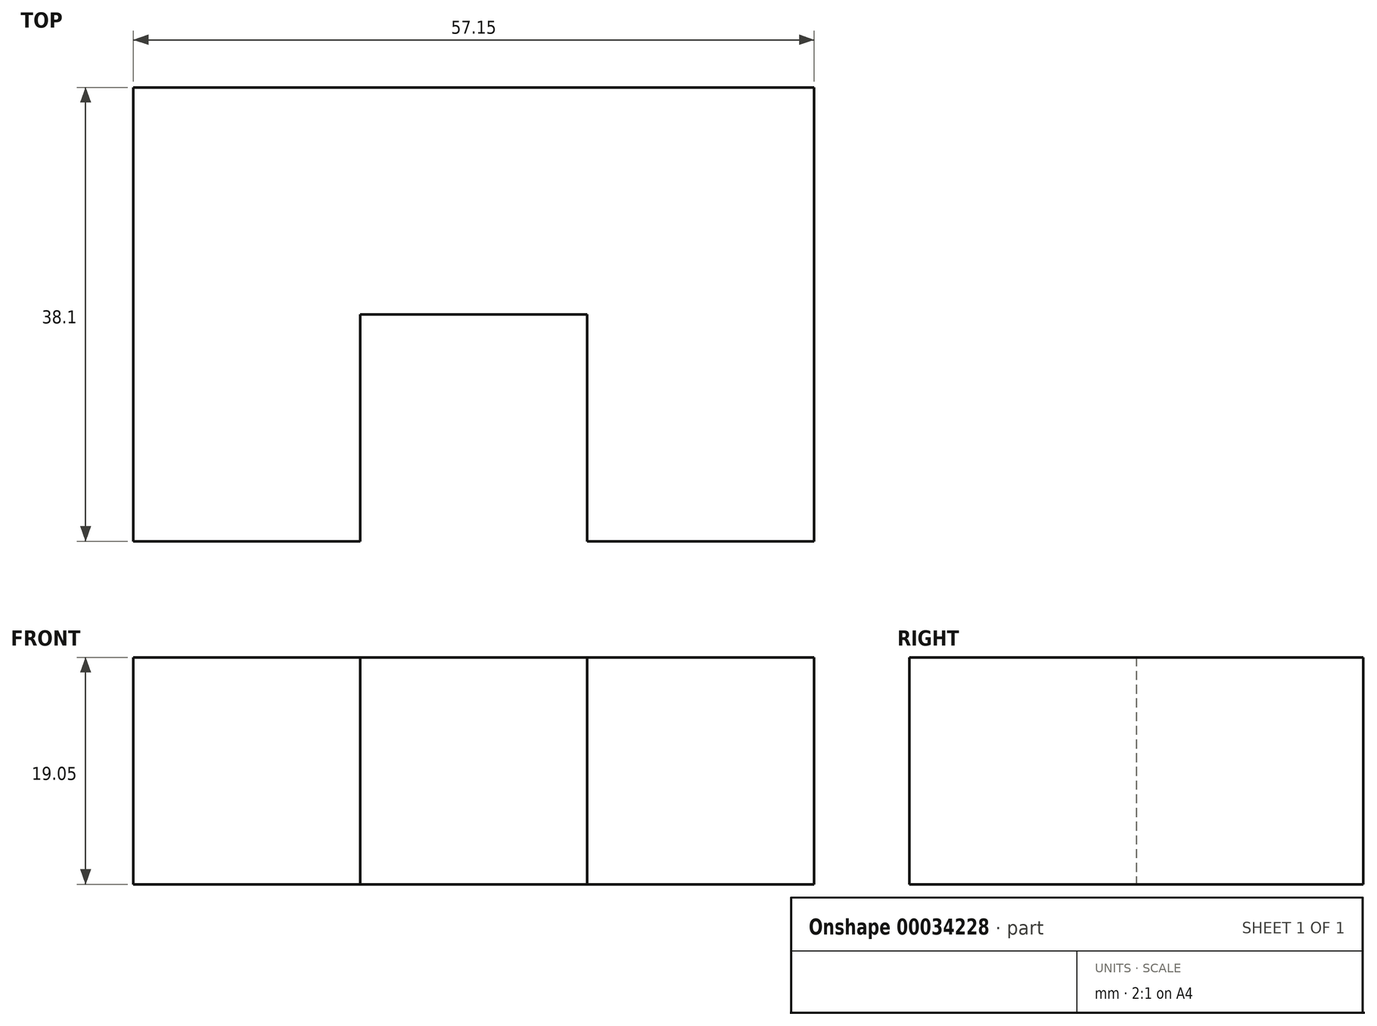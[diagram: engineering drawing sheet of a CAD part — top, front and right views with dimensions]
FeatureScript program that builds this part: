
annotation { "Feature Type Name" : "Feature", "Feature Type Description" : "" }
export const myFeature = defineFeature(function(context is Context, id is Id, definition is map)
    precondition{}
    {
        {
            var Q0;
            Q0=qCreatedBy(makeId("Top.planeOp"),FACE);
            var sketch = newSketch(context, id + "F0", { "sketchPlane" : qUnion([Q0])});
            skLineSegment(sketch, "E0.bottom", {"start": v(0, 0) * mm, "end": v(57.15, 0) * mm});
            skLineSegment(sketch, "E0.top", {"start": v(0, -19.05) * mm, "end": v(57.15, -19.05) * mm});
            skLineSegment(sketch, "E0.left", {"start": v(0, 0) * mm, "end": v(0, -19.05) * mm});
            skLineSegment(sketch, "E0.right", {"start": v(57.15, 0) * mm, "end": v(57.15, -19.05) * mm});
            skLineSegment(sketch, "E1.bottom", {"start": v(0, 0) * mm, "end": v(19.05, 0) * mm});
            skLineSegment(sketch, "E1.top", {"start": v(0, 19.05) * mm, "end": v(19.05, 19.05) * mm});
            skLineSegment(sketch, "E1.left", {"start": v(0, 0) * mm, "end": v(0, 19.05) * mm});
            skLineSegment(sketch, "E1.right", {"start": v(19.05, 0) * mm, "end": v(19.05, 19.05) * mm});
            skLineSegment(sketch, "E2.bottom", {"start": v(57.15, 0) * mm, "end": v(38.1, 0) * mm});
            skLineSegment(sketch, "E2.top", {"start": v(57.15, 19.05) * mm, "end": v(38.1, 19.05) * mm});
            skLineSegment(sketch, "E2.left", {"start": v(57.15, 0) * mm, "end": v(57.15, 19.05) * mm});
            skLineSegment(sketch, "E2.right", {"start": v(38.1, 0) * mm, "end": v(38.1, 19.05) * mm});
            skSolve(sketch);
        }
        {
            var Q0;
            Q0 = qSketchRegion(id + "F0", true);
            extrude(context, id + "F1", {"entities" : qUnion([Q0]), "depth" : 19.05 * mm});
        }
        {
            var Q0;
            Q0=makeQuery(id+"F1.opExtrude","SWEPT_BODY",BODY,{"disambiguationData":[OSD([sQuery(id+"F0.wireOp",EDGE,"E0.bottom"),sQuery(id+"F0.wireOp",EDGE,"E0.top"),sQuery(id+"F0.wireOp",EDGE,"E0.left"),sQuery(id+"F0.wireOp",EDGE,"E0.right"),sQuery(id+"F0.wireOp",EDGE,"E1.top"),sQuery(id+"F0.wireOp",EDGE,"E1.left"),sQuery(id+"F0.wireOp",EDGE,"E1.right"),sQuery(id+"F0.wireOp",EDGE,"E2.top"),sQuery(id+"F0.wireOp",EDGE,"E2.left"),sQuery(id+"F0.wireOp",EDGE,"E2.right")])]});
            var Q1;
            Q1=makeQuery(id+"F1.opExtrude","SWEPT_EDGE",EDGE,{"disambiguationData":[OSD([sQuery(id+"F0.wireOp",EDGE,"E0.top"),sQuery(id+"F0.wireOp",EDGE,"E0.left")])]});
            transform(context, id + "F2", {"entities" : qUnion([Q0]), "transformType" : TransformType.ROTATION, "transformAxis" : qUnion([Q1]), "angle" : 180 * degree, "makeCopy" : false});
        }
    });
